# Revit family: Haworth_MangasSpace_Rugs
name_source: partatom
category: Furniture
revit_build: Autodesk Revit 2018 (Build: 20170223_1515(x64)
units: mm (PartAtom-declared; Revit-internal decimal feet)

## family parameters
Always vertical = Yes
Cut with Voids When Loaded = No
OmniClass Number = 23.35.50.27.11.11
OmniClass Title = Access Floors, Frames
Room Calculation Point = No
Shared = No
Work Plane-Based = No

## types (2) — shared parameters
Actual Width = 63"
Inner Width = 39 51/128"
Manufacturer = Haworth
Model = HCGN-MS
Revision Number = 1
Size = Verify Final Dimensions w/ Haworth
Thickness = 1/4"
URL = http://www.haworth.com
URL - Product = https://www.haworth.com
Warranty = http://www.haworth.com

## per-type parameters (varying)
| type | Actual Length | Description | with Square |
| HCGN-MS2Q - with Square | 98 1/2" | Haworth Mangas Space Area Rug - With Squares | Yes |
| HCGN-MS1P - Plait | 63" | Haworth Mangas Space Plait Area Rug | No |

## geometry (parser evidence)
native form markers: Sweep x2
no freeform markers — native parametric forms only
